# Revit family: Diverter_Trim-American_Standard-Townsend-TU353740_Series
name_source: partatom
category: Plumbing Fixtures
units: mm (PartAtom-declared; Revit-internal decimal feet)

## family parameters
Cut with Voids When Loaded = No
Host = Face
OmniClass Number = 23.35.05.17.27
OmniClass Title = Trims, Edgings, Cappings
Part Type = Normal
Room Calculation Point = No
Round Connector Dimension = Use Diameter
Shared = Yes

## types (5) — shared parameters
2-Way Shared Cartridge #M970720-0070A = Yes
3-Way Shared Cartridge #M970730-0070A = No
3rd Outlet Water Connection Diameter = 0"
ADA Compliant = Yes
Assembly Code = D2020
CW Connection = Yes
CWFU = 3
Compliance Certifications = These products meet or exceed the following codes and standards: ASSE 1016, ASME A112.18.1, CSA B125.1
Default Elevation = 0"
Description = Townsend®2-Handle Integrated Shower Diverter Trim Only
Diameter = 9"
HW Connection = Yes
HWFU = 3
Installation Type = Wall Mounted
Manufacturer = American Standard
NPT Connection Size = 1/2"
Product Documentation Link = https://americanstandard.box.com
Product Page URL = https://www.americanstandard-us.com
RU521 Flash Rough Valve Body = Yes
RU531 Flash Rough Valve Body = No
URL = http://www.americanstandard-us.com
Valve Visibility = Yes
Vent Connection = No
WFU = 4
Waste Connection = No

## per-type parameters (varying)
| type | Finish | Material |
| TU353740.002 | Brass-American Standard-002-Polished Chrome | Brass-American Standard-002-Polished Chrome |
| TU353740.295 | Brass-American Standard-002-Polished Chrome | Brass-American Standard-002-Polished Chrome |
| TU353740.013 | Brass-American Standard-013-Polished Nickel | Brass-American Standard-013-Polished Nickel |
| TU353740.243 | Brass-American Standard-243-Matte Black | Brass-American Standard-243-Matte Black |
| TU353740.278 | Brass-American Standard-278-Legacy Bronze | Brass-American Standard-278-Legacy Bronze |

note: column(s) folded — value = type name in every type: Model

## geometry (parser evidence)
native form markers: Sweep x3
no freeform markers — native parametric forms only
